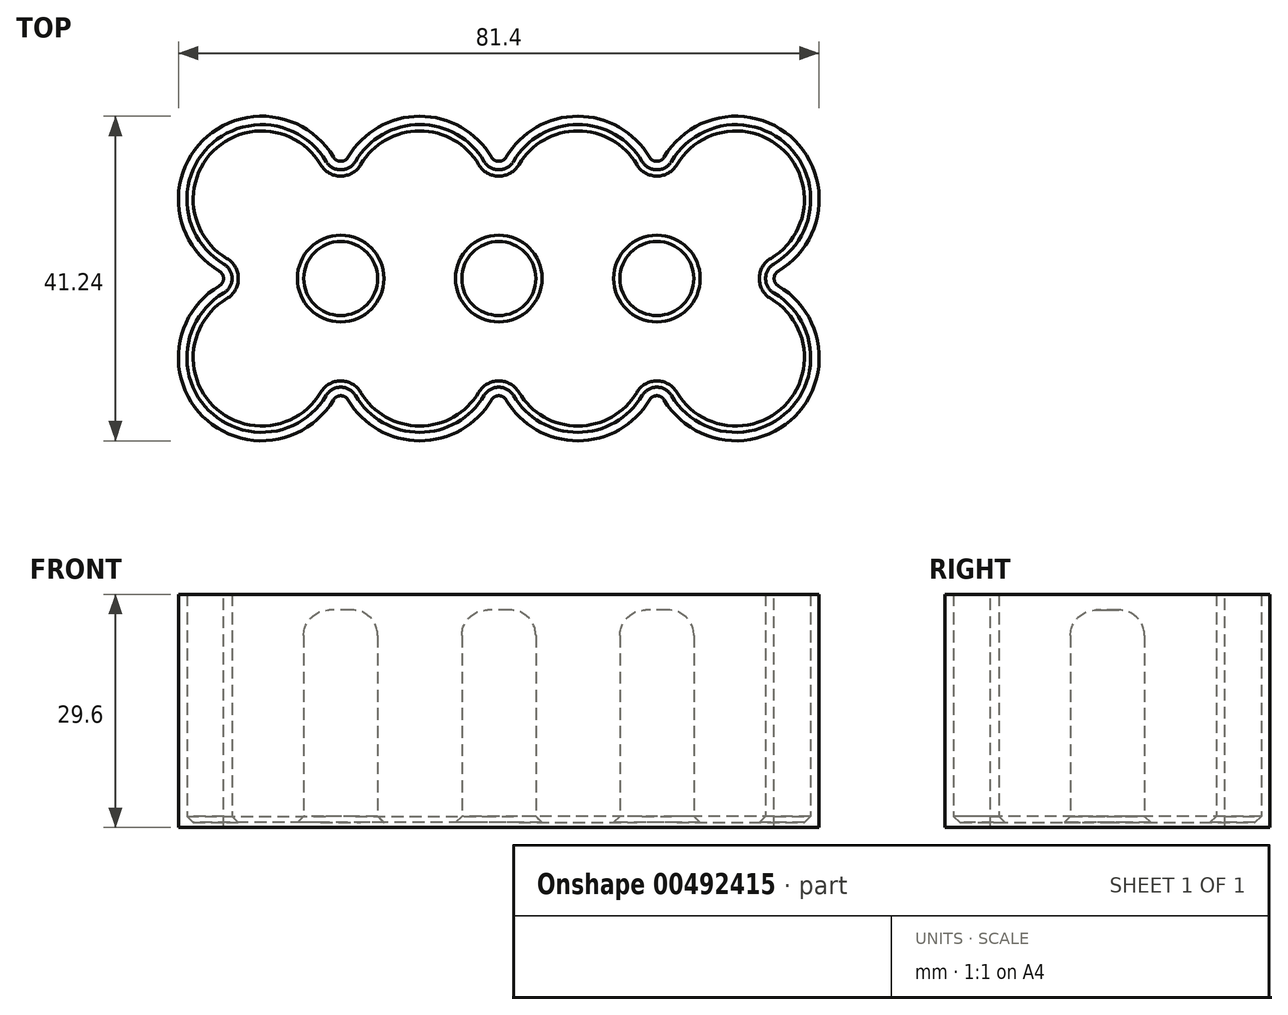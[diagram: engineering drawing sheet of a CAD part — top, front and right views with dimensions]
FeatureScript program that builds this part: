
annotation { "Feature Type Name" : "Feature", "Feature Type Description" : "" }
export const myFeature = defineFeature(function(context is Context, id is Id, definition is map)
    precondition{}
    {
        {
            var Q0;
            Q0=qCreatedBy(makeId("Top.planeOp"),FACE);
            var sketch = newSketch(context, id + "F0", { "sketchPlane" : qUnion([Q0])});
            skCircle(sketch, "E0", {"center": v(0, 0) * mm, "radius": 9.5 * mm, "construction": true});
            skCircle(sketch, "E1.0.1.0", {"center": v(0, 20.08) * mm, "radius": 9.5 * mm, "construction": true});
            skCircle(sketch, "E1.1.0.0", {"center": v(20.08, 0) * mm, "radius": 9.5 * mm, "construction": true});
            skCircle(sketch, "E1.1.1.0", {"center": v(20.08, 20.08) * mm, "radius": 9.5 * mm, "construction": true});
            skCircle(sketch, "E1.2.0.0", {"center": v(40.16, 0) * mm, "radius": 9.5 * mm, "construction": true});
            skCircle(sketch, "E1.2.1.0", {"center": v(40.16, 20.08) * mm, "radius": 9.5 * mm, "construction": true});
            skCircle(sketch, "E1.3.0.0", {"center": v(60.24, 0) * mm, "radius": 9.5 * mm, "construction": true});
            skCircle(sketch, "E1.3.1.0", {"center": v(60.24, 20.08) * mm, "radius": 9.5 * mm, "construction": true});
            skLineSegment(sketch, "E1.direction1", {"start": v(0, 0) * mm, "end": v(20.08, 0) * mm, "construction": true});
            skLineSegment(sketch, "E1.direction2", {"start": v(0, 0) * mm, "end": v(0, 20.08) * mm, "construction": true});
            skArc(sketch, "E2.0", {"start": v(10.04, 23.42) * mm, "mid": v(-7.48, 27.56) * mm, "end": v(-3.34, 10.04) * mm});
            skArc(sketch, "E3.0", {"start": v(63.58, 10.04) * mm, "mid": v(67.72, 27.56) * mm, "end": v(50.2, 23.42) * mm});
            skArc(sketch, "E4.0", {"start": v(50.2, -3.34) * mm, "mid": v(67.72, -7.48) * mm, "end": v(63.58, 10.04) * mm});
            skArc(sketch, "E5.0", {"start": v(30.12, -3.34) * mm, "mid": v(40.16, -10.58) * mm, "end": v(50.2, -3.34) * mm});
            skArc(sketch, "E6.0", {"start": v(10.04, -3.34) * mm, "mid": v(20.08, -10.58) * mm, "end": v(30.12, -3.34) * mm});
            skArc(sketch, "E7.0", {"start": v(-3.34, 10.04) * mm, "mid": v(-7.48, -7.48) * mm, "end": v(10.04, -3.34) * mm});
            skArc(sketch, "E8.trimOffspring", {"start": v(30.12, 23.42) * mm, "mid": v(20.08, 30.66) * mm, "end": v(10.04, 23.42) * mm});
            skArc(sketch, "E9.trimOffspring", {"start": v(50.2, 23.42) * mm, "mid": v(40.16, 30.66) * mm, "end": v(30.12, 23.42) * mm});
            skSolve(sketch);
        }
        {
            var Q0;
            Q0 = qSketchRegion(id + "F0", true);
            extrude(context, id + "F1", {"entities" : qUnion([Q0]), "depth" : 0.6 * mm});
        }
        {
            var Q0;
            Q0=makeQuery(id+"F1.opExtrude","SWEPT_EDGE",EDGE,{"disambiguationData":[OSD([sQuery(id+"F0.wireOp",EDGE,"E6.0"),sQuery(id+"F0.wireOp",EDGE,"E7.0")])]});
            var Q1;
            Q1=makeQuery(id+"F1.opExtrude","SWEPT_EDGE",EDGE,{"disambiguationData":[OSD([sQuery(id+"F0.wireOp",EDGE,"E5.0"),sQuery(id+"F0.wireOp",EDGE,"E6.0")])]});
            var Q2;
            Q2=makeQuery(id+"F1.opExtrude","SWEPT_EDGE",EDGE,{"disambiguationData":[OSD([sQuery(id+"F0.wireOp",EDGE,"E4.0"),sQuery(id+"F0.wireOp",EDGE,"E5.0")])]});
            var Q3;
            Q3=makeQuery(id+"F1.opExtrude","SWEPT_EDGE",EDGE,{"disambiguationData":[OSD([sQuery(id+"F0.wireOp",EDGE,"E3.0"),sQuery(id+"F0.wireOp",EDGE,"E4.0")])]});
            var Q4;
            Q4=makeQuery(id+"F1.opExtrude","SWEPT_EDGE",EDGE,{"disambiguationData":[OSD([sQuery(id+"F0.wireOp",EDGE,"E3.0"),sQuery(id+"F0.wireOp",EDGE,"E9.trimOffspring")])]});
            var Q5;
            Q5=makeQuery(id+"F1.opExtrude","SWEPT_EDGE",EDGE,{"disambiguationData":[OSD([sQuery(id+"F0.wireOp",EDGE,"E8.trimOffspring"),sQuery(id+"F0.wireOp",EDGE,"E9.trimOffspring")])]});
            var Q6;
            Q6=makeQuery(id+"F1.opExtrude","SWEPT_EDGE",EDGE,{"disambiguationData":[OSD([sQuery(id+"F0.wireOp",EDGE,"E2.0"),sQuery(id+"F0.wireOp",EDGE,"E8.trimOffspring")])]});
            var Q7;
            Q7=makeQuery(id+"F1.opExtrude","SWEPT_EDGE",EDGE,{"disambiguationData":[OSD([sQuery(id+"F0.wireOp",EDGE,"E2.0"),sQuery(id+"F0.wireOp",EDGE,"E7.0")])]});
            fillet(context, id + "F2", {"entities" : qUnion([Q0, Q1, Q2, Q3, Q4, Q5, Q6, Q7]), "radius" : 1.08 * mm, "tangentPropagation" : true, "allowEdgeOverflow" : false});
        }
        {
            var Q0;
            Q0=makeQuery(id+"F1.opExtrude","CAP_FACE",FACE,{"disambiguationData":[OSD([sQuery(id+"F0.wireOp",EDGE,"E2.0"),sQuery(id+"F0.wireOp",EDGE,"E3.0"),sQuery(id+"F0.wireOp",EDGE,"E4.0"),sQuery(id+"F0.wireOp",EDGE,"E5.0"),sQuery(id+"F0.wireOp",EDGE,"E6.0"),sQuery(id+"F0.wireOp",EDGE,"E7.0"),sQuery(id+"F0.wireOp",EDGE,"E8.trimOffspring"),sQuery(id+"F0.wireOp",EDGE,"E9.trimOffspring")])],"isStart":false});
            var sketch = newSketch(context, id + "F3", { "sketchPlane" : qUnion([Q0])});
            skArc(sketch, "E10.0.0", {"start": v(9.11, 25.46) * mm, "mid": v(-7.48, 27.56) * mm, "end": v(-5.38, 10.97) * mm});
            skArc(sketch, "E10.0.1", {"start": v(-5.38, 10.97) * mm, "mid": v(-4.85, 10.04) * mm, "end": v(-5.38, 9.11) * mm});
            skArc(sketch, "E10.0.2", {"start": v(-5.38, 9.11) * mm, "mid": v(-7.48, -7.48) * mm, "end": v(9.11, -5.38) * mm});
            skArc(sketch, "E10.0.3", {"start": v(9.11, -5.38) * mm, "mid": v(10.04, -4.85) * mm, "end": v(10.97, -5.38) * mm});
            skArc(sketch, "E10.0.4", {"start": v(10.97, -5.38) * mm, "mid": v(20.08, -10.58) * mm, "end": v(29.2, -5.38) * mm});
            skArc(sketch, "E10.0.5", {"start": v(29.2, -5.38) * mm, "mid": v(30.12, -4.85) * mm, "end": v(31.05, -5.38) * mm});
            skArc(sketch, "E10.0.6", {"start": v(31.05, -5.38) * mm, "mid": v(40.16, -10.58) * mm, "end": v(49.27, -5.38) * mm});
            skArc(sketch, "E10.0.7", {"start": v(49.27, -5.38) * mm, "mid": v(50.2, -4.85) * mm, "end": v(51.13, -5.38) * mm});
            skArc(sketch, "E10.0.8", {"start": v(51.13, -5.38) * mm, "mid": v(67.72, -7.48) * mm, "end": v(65.62, 9.11) * mm});
            skArc(sketch, "E10.0.9", {"start": v(65.62, 9.11) * mm, "mid": v(65.09, 10.04) * mm, "end": v(65.62, 10.97) * mm});
            skArc(sketch, "E10.0.10", {"start": v(65.62, 10.97) * mm, "mid": v(67.72, 27.56) * mm, "end": v(51.13, 25.46) * mm});
            skArc(sketch, "E10.0.11", {"start": v(51.13, 25.46) * mm, "mid": v(50.2, 24.93) * mm, "end": v(49.27, 25.46) * mm});
            skArc(sketch, "E10.0.12", {"start": v(49.27, 25.46) * mm, "mid": v(40.16, 30.66) * mm, "end": v(31.05, 25.46) * mm});
            skArc(sketch, "E10.0.13", {"start": v(31.05, 25.46) * mm, "mid": v(30.12, 24.93) * mm, "end": v(29.2, 25.46) * mm});
            skArc(sketch, "E10.0.14", {"start": v(29.2, 25.46) * mm, "mid": v(20.08, 30.66) * mm, "end": v(10.97, 25.46) * mm});
            skArc(sketch, "E10.0.15", {"start": v(10.97, 25.46) * mm, "mid": v(10.04, 24.93) * mm, "end": v(9.11, 25.46) * mm});
            skArc(sketch, "E11.0", {"start": v(11.9, 24.91) * mm, "mid": v(10.04, 23.85) * mm, "end": v(8.18, 24.91) * mm});
            skArc(sketch, "E11.1", {"start": v(28.26, 24.91) * mm, "mid": v(20.08, 29.58) * mm, "end": v(11.9, 24.91) * mm});
            skArc(sketch, "E11.2", {"start": v(31.98, 24.91) * mm, "mid": v(30.12, 23.85) * mm, "end": v(28.26, 24.91) * mm});
            skArc(sketch, "E11.3", {"start": v(48.34, 24.91) * mm, "mid": v(40.16, 29.58) * mm, "end": v(31.98, 24.91) * mm});
            skArc(sketch, "E11.4", {"start": v(52.06, 24.91) * mm, "mid": v(50.2, 23.85) * mm, "end": v(48.34, 24.91) * mm});
            skArc(sketch, "E11.5", {"start": v(11.9, -4.83) * mm, "mid": v(20.08, -9.5) * mm, "end": v(28.26, -4.83) * mm});
            skArc(sketch, "E11.6", {"start": v(8.18, -4.83) * mm, "mid": v(10.04, -3.77) * mm, "end": v(11.9, -4.83) * mm});
            skArc(sketch, "E11.7", {"start": v(-4.83, 8.18) * mm, "mid": v(-6.72, -6.72) * mm, "end": v(8.18, -4.83) * mm});
            skArc(sketch, "E11.8", {"start": v(-4.83, 11.9) * mm, "mid": v(-3.77, 10.04) * mm, "end": v(-4.83, 8.18) * mm});
            skArc(sketch, "E11.9", {"start": v(28.26, -4.83) * mm, "mid": v(30.12, -3.77) * mm, "end": v(31.98, -4.83) * mm});
            skArc(sketch, "E11.10", {"start": v(31.98, -4.83) * mm, "mid": v(40.16, -9.5) * mm, "end": v(48.34, -4.83) * mm});
            skArc(sketch, "E11.11", {"start": v(48.34, -4.83) * mm, "mid": v(50.2, -3.77) * mm, "end": v(52.06, -4.83) * mm});
            skArc(sketch, "E11.12", {"start": v(52.06, -4.83) * mm, "mid": v(66.96, -6.72) * mm, "end": v(65.07, 8.18) * mm});
            skArc(sketch, "E11.13", {"start": v(65.07, 8.18) * mm, "mid": v(64, 10.04) * mm, "end": v(65.07, 11.9) * mm});
            skArc(sketch, "E11.14", {"start": v(8.18, 24.91) * mm, "mid": v(-6.72, 26.8) * mm, "end": v(-4.83, 11.9) * mm});
            skArc(sketch, "E11.15", {"start": v(65.07, 11.9) * mm, "mid": v(66.96, 26.8) * mm, "end": v(52.06, 24.91) * mm});
            skSolve(sketch);
        }
        {
            var Q0;
            Q0 = qSketchRegion(id + "F3", true);
            extrude(context, id + "F4", {"entities" : qUnion([Q0]), "operationType" : NewBodyOperationType.ADD, "depth" : 29 * mm});
        }
        {
            var Q0;
            Q0=makeQuery(id+"F1.opExtrude","CAP_FACE",FACE,{"disambiguationData":[OSD([sQuery(id+"F0.wireOp",EDGE,"E2.0"),sQuery(id+"F0.wireOp",EDGE,"E3.0"),sQuery(id+"F0.wireOp",EDGE,"E4.0"),sQuery(id+"F0.wireOp",EDGE,"E5.0"),sQuery(id+"F0.wireOp",EDGE,"E6.0"),sQuery(id+"F0.wireOp",EDGE,"E7.0"),sQuery(id+"F0.wireOp",EDGE,"E8.trimOffspring"),sQuery(id+"F0.wireOp",EDGE,"E9.trimOffspring")])],"isStart":false});
            var sketch = newSketch(context, id + "F5", { "sketchPlane" : qUnion([Q0])});
            skCircle(sketch, "E12", {"center": v(10.04, 10.04) * mm, "radius": 4.7 * mm});
            skCircle(sketch, "E13", {"center": v(30.12, 10.04) * mm, "radius": 4.7 * mm});
            skCircle(sketch, "E14", {"center": v(50.2, 10.04) * mm, "radius": 4.7 * mm});
            skSolve(sketch);
        }
        {
            var Q0;
            Q0 = qSketchRegion(id + "F5", true);
            extrude(context, id + "F6", {"entities" : qUnion([Q0]), "operationType" : NewBodyOperationType.ADD, "depth" : 27 * mm});
        }
        {
            var Q0;
            Q0=makeQuery(id+"F6.opExtrude","CAP_FACE",FACE,{"disambiguationData":[OSD([sQuery(id+"F5.wireOp",EDGE,"E12")])],"isStart":false});
            var Q1;
            Q1=makeQuery(id+"F6.opExtrude","CAP_EDGE",EDGE,{"disambiguationData":[OSD([sQuery(id+"F5.wireOp",EDGE,"E13")])],"isStart":false});
            var Q2;
            Q2=makeQuery(id+"F6.opExtrude","CAP_EDGE",EDGE,{"disambiguationData":[OSD([sQuery(id+"F5.wireOp",EDGE,"E14")])],"isStart":false});
            fillet(context, id + "F7", {"entities" : qUnion([Q0, Q1, Q2]), "radius" : 3.24 * mm, "tangentPropagation" : true, "allowEdgeOverflow" : false});
        }
        {
            var Q0;
            Q0=makeQuery(id+"F1.opExtrude","CAP_FACE",FACE,{"disambiguationData":[OSD([sQuery(id+"F0.wireOp",EDGE,"E2.0"),sQuery(id+"F0.wireOp",EDGE,"E3.0"),sQuery(id+"F0.wireOp",EDGE,"E4.0"),sQuery(id+"F0.wireOp",EDGE,"E5.0"),sQuery(id+"F0.wireOp",EDGE,"E6.0"),sQuery(id+"F0.wireOp",EDGE,"E7.0"),sQuery(id+"F0.wireOp",EDGE,"E8.trimOffspring"),sQuery(id+"F0.wireOp",EDGE,"E9.trimOffspring")])],"isStart":false});
            chamfer(context, id + "F8", {"entities" : qUnion([Q0]), "width" : 0.8 * mm, "tangentPropagation" : true});
        }
    });
